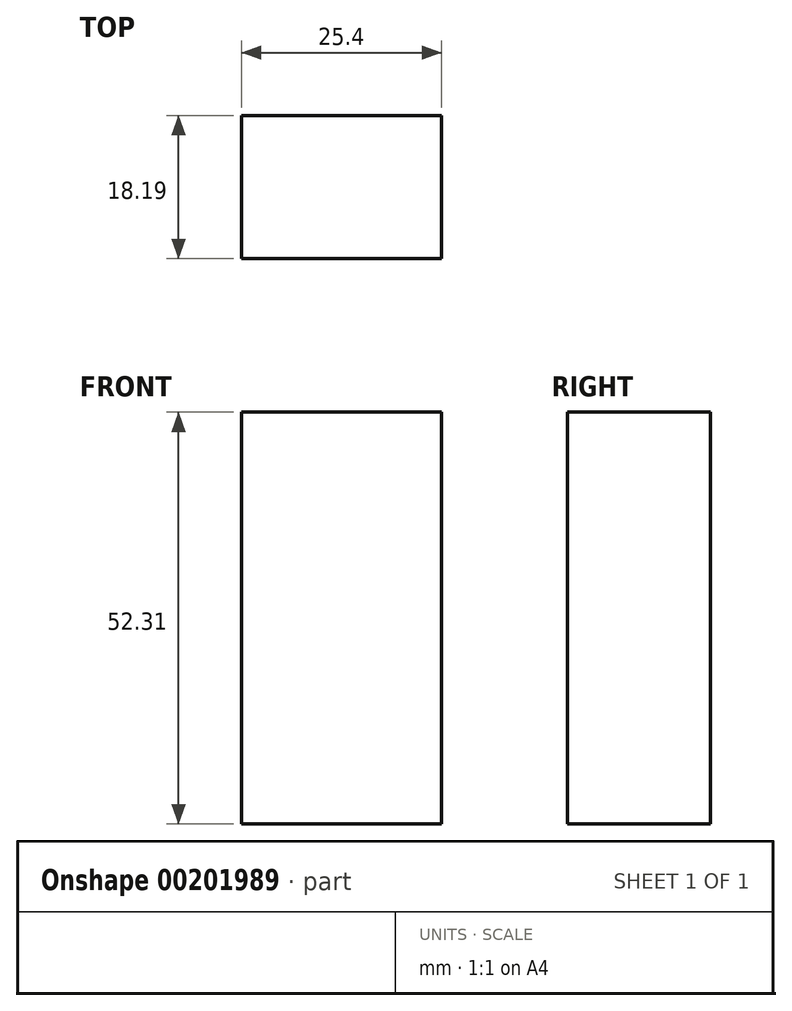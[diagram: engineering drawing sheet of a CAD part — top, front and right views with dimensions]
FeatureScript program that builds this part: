
annotation { "Feature Type Name" : "Feature", "Feature Type Description" : "" }
export const myFeature = defineFeature(function(context is Context, id is Id, definition is map)
    precondition{}
    {
        {
            var Q0;
            Q0=qCreatedBy(makeId("Right.planeOp"),FACE);
            var sketch = newSketch(context, id + "F0", { "sketchPlane" : qUnion([Q0])});
            skLineSegment(sketch, "E0.bottom", {"start": v(23.2, 27.52) * mm, "end": v(41.39, 27.52) * mm});
            skLineSegment(sketch, "E0.top", {"start": v(23.2, -24.79) * mm, "end": v(41.39, -24.79) * mm});
            skLineSegment(sketch, "E0.left", {"start": v(23.2, 27.52) * mm, "end": v(23.2, -24.79) * mm});
            skLineSegment(sketch, "E0.right", {"start": v(41.39, 27.52) * mm, "end": v(41.39, -24.79) * mm});
            skSolve(sketch);
        }
        {
            var Q0;
            Q0=makeQuery(id+"F0.imprint","IMPRINT",FACE,{"disambiguationData":[TD([[makeQuery(id+"F0.imprint","IMPRINT",EDGE,{"derivedFrom":sQuery(id+"F0.wireOp",EDGE,"E0.bottom")}),-1.0]])]});
            extrude(context, id + "F1", {"entities" : qUnion([Q0]), "depth" : 25.4 * mm});
        }
    });
